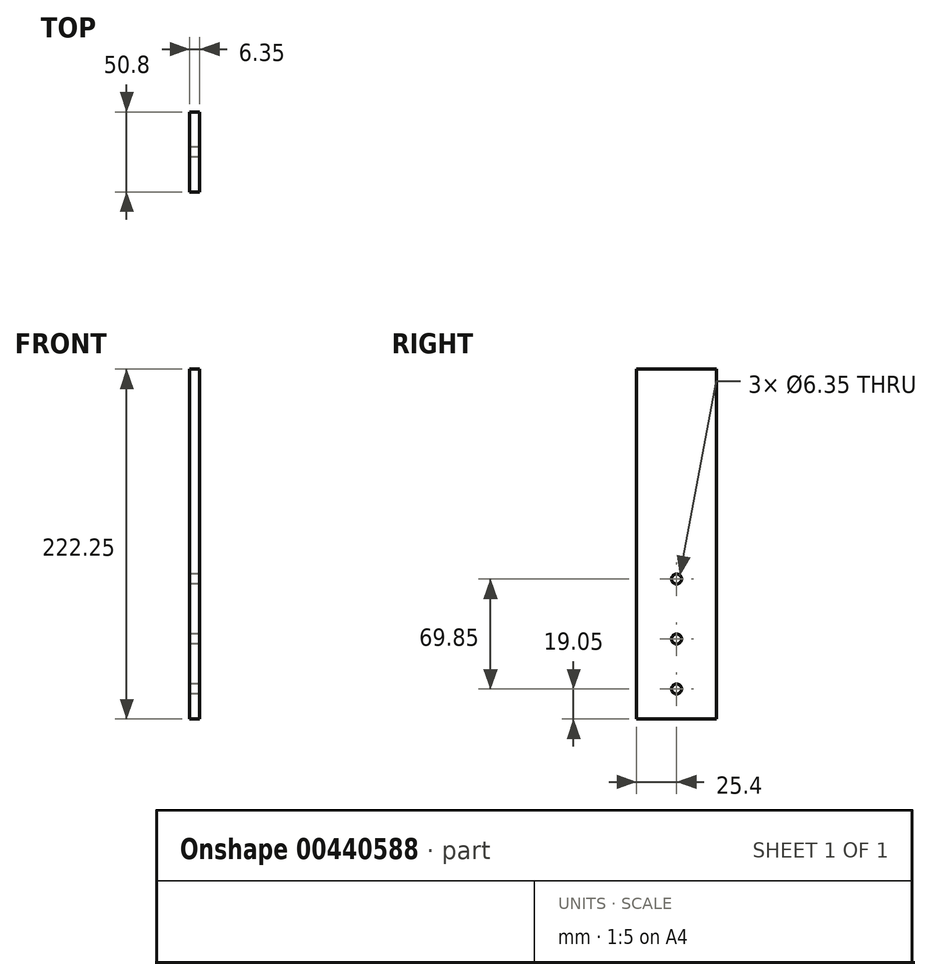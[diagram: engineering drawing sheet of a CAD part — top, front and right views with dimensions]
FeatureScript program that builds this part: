
annotation { "Feature Type Name" : "Feature", "Feature Type Description" : "" }
export const myFeature = defineFeature(function(context is Context, id is Id, definition is map)
    precondition{}
    {
        {
            var Q0;
            Q0=qCreatedBy(makeId("Right.planeOp"),FACE);
            var sketch = newSketch(context, id + "F0", { "sketchPlane" : qUnion([Q0])});
            skLineSegment(sketch, "E0.bottom", {"start": v(25.4, 0) * mm, "end": v(-25.4, 0) * mm});
            skLineSegment(sketch, "E0.top", {"start": v(25.4, 222.25) * mm, "end": v(-25.4, 222.25) * mm});
            skLineSegment(sketch, "E0.left", {"start": v(25.4, 0) * mm, "end": v(25.4, 222.25) * mm});
            skLineSegment(sketch, "E0.right", {"start": v(-25.4, 0) * mm, "end": v(-25.4, 222.25) * mm});
            skPoint(sketch, "E0.middle", {"position": v(0, 111.12) * mm});
            skCircle(sketch, "E1", {"center": v(0, 88.9) * mm, "radius": 3.18 * mm});
            skCircle(sketch, "E2", {"center": v(0, 19.05) * mm, "radius": 3.18 * mm});
            skCircle(sketch, "E3", {"center": v(0, 50.8) * mm, "radius": 3.18 * mm});
            skSolve(sketch);
        }
        {
            var Q0;
            Q0=makeQuery(id+"F0.imprint","IMPRINT",FACE,{"disambiguationData":[TD([[makeQuery(id+"F0.imprint","IMPRINT",EDGE,{"derivedFrom":sQuery(id+"F0.wireOp",EDGE,"E0.bottom")}),-1.0]])]});
            extrude(context, id + "F1", {"entities" : qUnion([Q0]), "depth" : 6.35 * mm});
        }
    });
